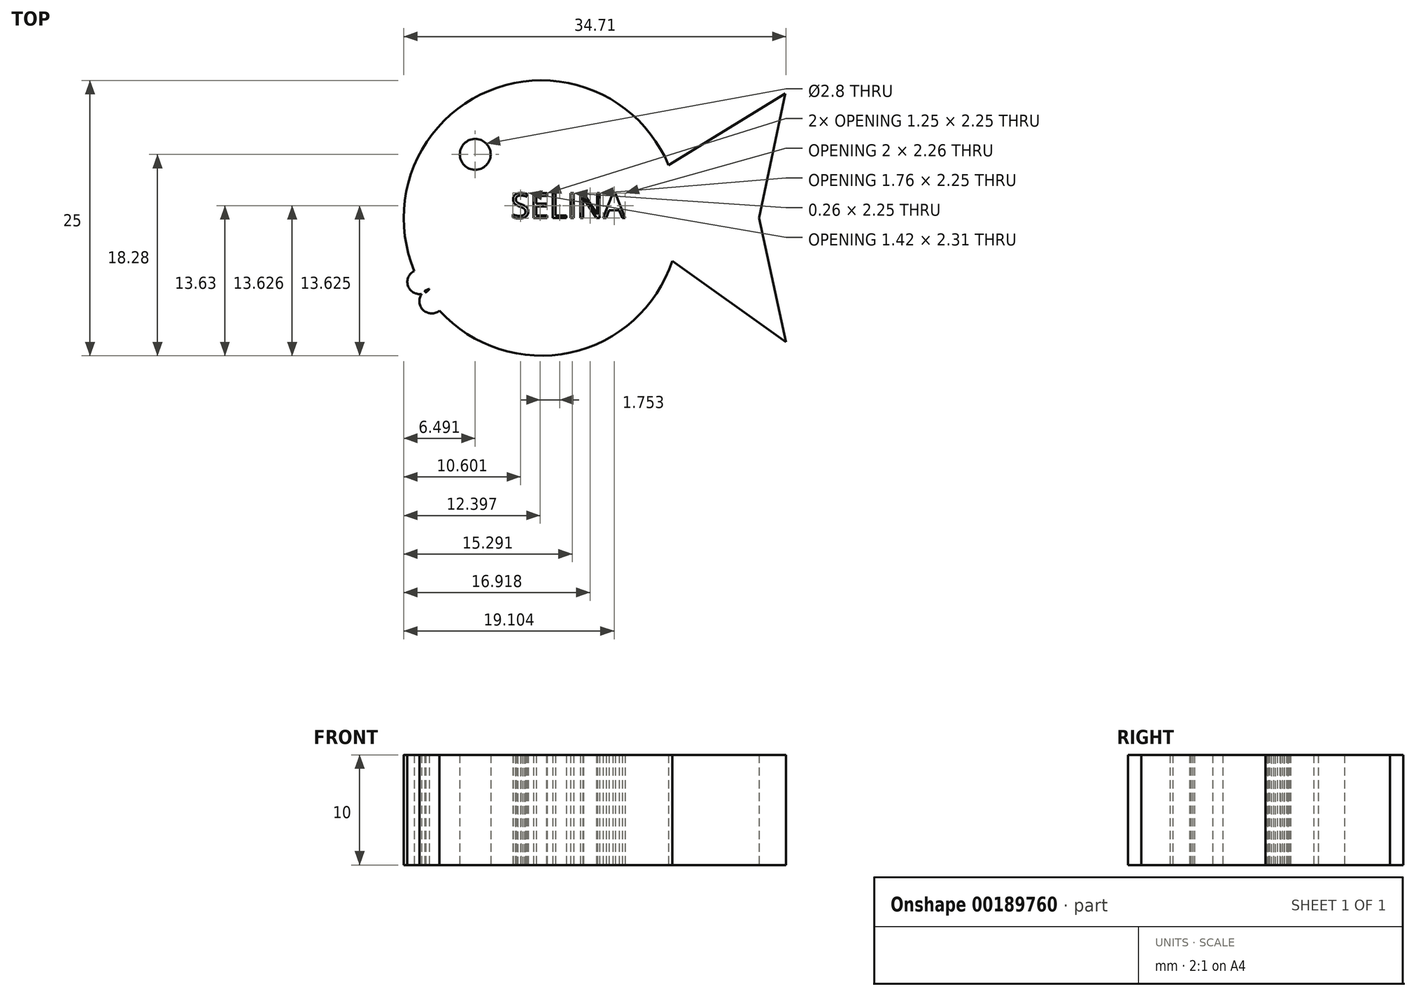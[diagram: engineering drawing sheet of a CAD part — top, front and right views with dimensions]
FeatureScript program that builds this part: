
annotation { "Feature Type Name" : "Feature", "Feature Type Description" : "" }
export const myFeature = defineFeature(function(context is Context, id is Id, definition is map)
    precondition{}
    {
        {
            var Q0;
            Q0=qCreatedBy(makeId("Top.planeOp"),FACE);
            var sketch = newSketch(context, id + "F0", { "sketchPlane" : qUnion([Q0])});
            skCircle(sketch, "E0", {"center": v(3.77, 0) * mm, "radius": 12.5 * mm});
            skCircle(sketch, "E1", {"center": v(-2.24, 5.78) * mm, "radius": 1.4 * mm});
            skLineSegment(sketch, "E2", {"start": v(15.32, 4.79) * mm, "end": v(25.92, 11.3) * mm});
            skLineSegment(sketch, "E3", {"start": v(25.92, 11.3) * mm, "end": v(23.53, 0) * mm});
            skLineSegment(sketch, "E4", {"start": v(23.53, 0) * mm, "end": v(25.98, -11.27) * mm});
            skLineSegment(sketch, "E5", {"start": v(25.98, -11.27) * mm, "end": v(15.65, -3.89) * mm});
            skText(sketch, "E6", { "text": "SELINA", "fontName": "OpenSans-Regular.ttf"});
            skCircle(sketch, "E7", {"center": v(-7.3, -5.8) * mm, "radius": 1.1 * mm});
            skCircle(sketch, "E8", {"center": v(-6.2, -7.55) * mm, "radius": 1.12 * mm});
            const initialGuessF0  = {"E6": [0.001, 0, 1, 0, 0.00227]};
            skSetInitialGuess(sketch, initialGuessF0);
            skSolve(sketch);
        }
        {
            var Q0;
            Q0 = qSketchRegion(id + "F0", true);
            extrude(context, id + "F1", {"entities" : qUnion([Q0]), "depth" : 10 * mm});
        }
    });
